# Revit family: AVPL_DN15_RFA
name_source: partatom
category: Pipe Accessories
units: mm (PartAtom-declared; Revit-internal decimal feet)

## family parameters
Always vertical = Yes
Cut with Voids When Loaded = No
OmniClass Number = 23.65.55.14.17
OmniClass Title = Adjusting/Controlling Valves for Liquid Services
Part Type = Valve - Breaks Into
Round Connector Dimension = Use Diameter
Shared = No
Work Plane-Based = No

## types (2) — shared parameters
Connection = External Thread
D = 15 mm  [stored 0.0492126 ft]
Description = Differential Pressure Controller
Differential Pressure Setting Range = 0.05-0.25 bar
IfcExportAs = IfcValveType
IfcExportType = AVPL
LOD 200 = No
LOD 350 = Yes
Manufacturer = Danfoss
Max Differential Pressure = 4.5 bar
Max Medium Temperature = 120 °C
Min Medium Temperature = 2 °C
Nominal Pressure = PN 16
URL = https://store.danfoss.com
Valve Body Material = Danfoss Brass (DZR)

## per-type parameters (varying)
| type | Kvs | Model | Model Type | Weight |
| AVPL_DN15_Kvs1.0_003L5030 | 1.0 m³/h | 003L5030 | AVPL_DN15_Kvs1.0 | 0.64 kg |
| AVPL_DN15_Kvs1.6_003L5031 | 1.6 m³/h | 003L5031 | AVPL_DN15_Kvs1.6 | 0.69 kg |

note: [stored X ft] marks values corroborated as IEEE doubles in the binary element streams (Revit-internal decimal feet)

## geometry (parser evidence)
native form markers: Sweep x4
no freeform markers — native parametric forms only
